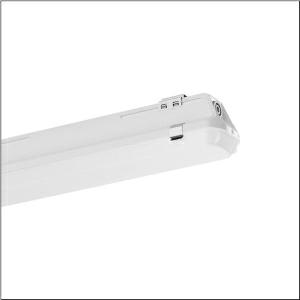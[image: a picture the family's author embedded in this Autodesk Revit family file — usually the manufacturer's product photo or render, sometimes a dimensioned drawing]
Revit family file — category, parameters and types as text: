
# Revit family: monsun_r__21_51fb10dp660b_51d9
name_source: partatom
category: Lighting Fixtures
units: mm (PartAtom-declared; Revit-internal decimal feet)

## family parameters
Cut with Voids When Loaded = No
Host = Face
Light Source = No
Part Type = Normal
Room Calculation Point = No
Round Connector Dimension = Use Diameter
Shared = No

## types (1)
- --- (1 x LED, 6060 lm, 39.4 W, 6500K)
    Apparent Load = 39 VA
    CIE Flux Codes = 47 77 93 94 100
    Color Rendering = 80
    Color Temperature = 6500K
    Default Elevation = 1800 mm
    Description = Monsun® 21, damp-proof luminaire, chain hanger, primary optical cover: enclosure, of PMMA, light emission: direct distribution, primary light characteristic: symmetric, installation type: suspended mounting, surface-mounted, horizontal mounting, vertical mounting, LED, rated luminous flux: 6.060lm, luminous efficacy: 154lm/W, light colour: 865, colour temperature: 6500K, control gear: ECG DALI, with terminal, 5-pole, max. 2.5mm², mains connection: 220..240V, AC, 50/60Hz, rated input power: 39W, housing, of glass-fibre reinforced polyester, uncoated, bright grey, incl. chain hanger, length: 1.590mm, width: 90mm, height: 88mm, clip for enclosure, of stainless steel (V2A), ceiling mounting element, of stainless steel (V2A), chain hanger, of stainless steel (V2A), protection rating (complete): IP66, insulation class (complete): insulation class I (protective earthing), certification: CE, ENEC, VDE, UKCA, protection symbol: D, impact resistance: IK04, permissible operating ambient temperature: -25..+35°C, standard: EN 50419, EN 60598-2-1, corresponds to IFS (International Featured Standards) requirements for safety and quality in the food industry, for indoor or canopied outdoor use, no direct snow, no direct sun, no direct rain, contact your sales advisor before using the luminaires in applications with unclear chemical exposure, large temperature fluctuations or condensation-forming humidity, LABS conformity tested according to VDMA 24364:2018-05, packaging unit: 1 piece
    Height = 89 mm
    Lamp = 1 x LED
    Lamp Light Flux = 6060 lm
    Lamp Power = 39.4 W
    Lamp count = 1
    Length = 1590 mm
    Luminous efficacy = 154 lm/W
    Manufacturer = Siteco
    ModVariant = No
    Model = 51FB10DP660B
    Mounting Place = Ceiling
    Mounting Type = Surface mounted
    Number of Poles = 1
    OnlyDefault = Yes
    Power Factor = 1
    Product Name = Monsun® 21
    Product group = damp-proof luminaire
    ProductGroupID = 300
    Protection Class = Protection class I
    Protection Degree = IP 66
    RLX_Detail_Level = 1
    RLX_Emergency_Light_Flux = 0 lm
    RLX_Emergency_Type = 0
    RLX_Emergency_Type_DB = No
    RlxData = <blob elided: 92077 chars, md5=33ff6117>
    Socket = socket
    Standby Power = 0 W
    System Light Flux = 6060 lm
    System Power = 39 W
    Type Comments = factory setting: luminous flux: 100 % | dim-lin: 254 | 261 mA
    Type Image = l_1319656.jpg
    URL = http://relux.com
    VarID = @adj_171175
    Voltage = 0 V
    Weight = 0.00 kg
    Width = 90 mm

## geometry (parser evidence)
native form markers: Blend x4, Sweep x15
no freeform markers — native parametric forms only
